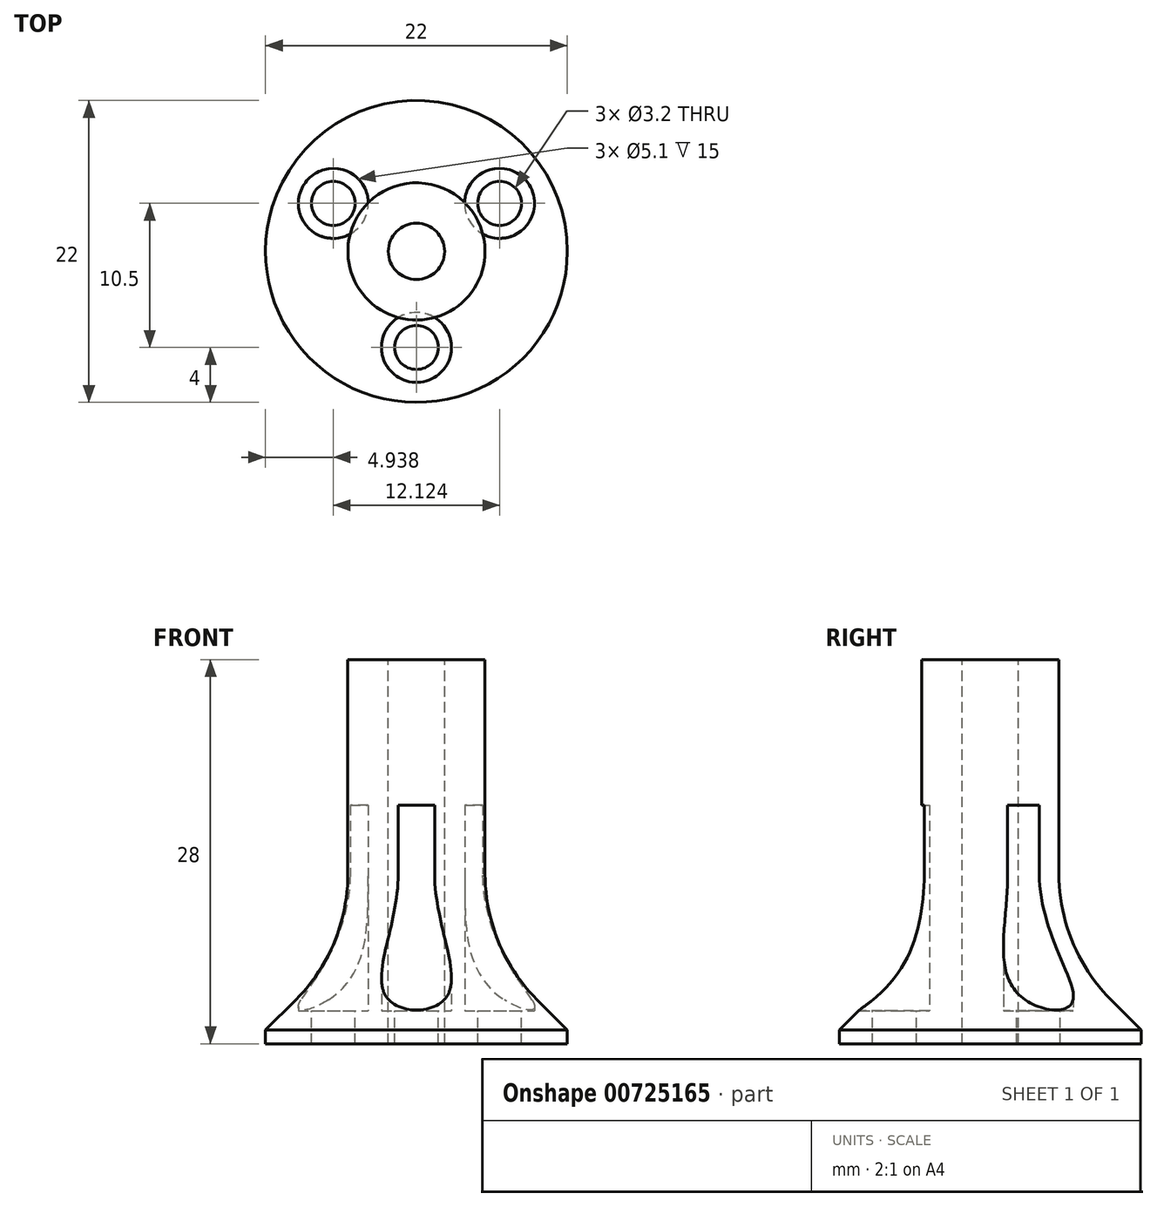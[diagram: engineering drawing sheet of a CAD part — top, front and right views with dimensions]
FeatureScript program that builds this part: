
annotation { "Feature Type Name" : "Feature", "Feature Type Description" : "" }
export const myFeature = defineFeature(function(context is Context, id is Id, definition is map)
    precondition{}
    {
        {
            var Q0;
            Q0=qCreatedBy(makeId("Top.planeOp"),FACE);
            var sketch = newSketch(context, id + "F0", { "sketchPlane" : qUnion([Q0])});
            skCircle(sketch, "E0", {"center": v(0, 0) * mm, "radius": 13 * mm});
            skSolve(sketch);
        }
        {
            var Q0;
            Q0 = qSketchRegion(id + "F0", true);
            extrude(context, id + "F1", {"entities" : qUnion([Q0]), "depth" : 6 * mm, "offsetDistance" : 25 * mm});
        }
        {
            var Q0;
            Q0=makeQuery(id+"F1.opExtrude","CAP_FACE",FACE,{"disambiguationData":[OSD([sQuery(id+"F0.wireOp",EDGE,"E0")])],"isStart":false});
            var sketch = newSketch(context, id + "F2", { "sketchPlane" : qUnion([Q0])});
            skCircle(sketch, "E1", {"center": v(0, 0) * mm, "radius": 5 * mm});
            skSolve(sketch);
        }
        {
            var Q0;
            Q0=makeQuery(id+"F2.imprint","IMPRINT",FACE,{"disambiguationData":[TD([[makeQuery(id+"F2.imprint","IMPRINT",EDGE,{"derivedFrom":sQuery(id+"F2.wireOp",EDGE,"E1")}),1.0]])]});
            extrude(context, id + "F3", {"entities" : qUnion([Q0]), "operationType" : NewBodyOperationType.ADD, "depth" : 21 * mm, "offsetDistance" : 25 * mm});
        }
        {
            var Q0;
            Q0=makeQuery(id+"F1.opExtrude","CAP_EDGE",EDGE,{"disambiguationData":[OSD([sQuery(id+"F0.wireOp",EDGE,"E0")])],"isStart":false});
            chamfer(context, id + "F4", {"entities" : qUnion([Q0]), "width" : 8 * mm, "tangentPropagation" : true});
        }
        {
            var Q0;
            Q0=makeQuery(id+"F4.opChamfer","BLEND_EDGE",EDGE,{"blendedFrom":[makeQuery(id+"F1.opExtrude","CAP_EDGE",EDGE,{"disambiguationData":[OSD([sQuery(id+"F0.wireOp",EDGE,"E0")])],"isStart":false}),makeQuery(id+"F3.opExtrude","SWEPT_FACE",FACE,{"disambiguationData":[OSD([sQuery(id+"F2.wireOp",EDGE,"E1")])]})],"blendedInto":[makeQuery(id+"F3.opExtrude","SWEPT_FACE",FACE,{"disambiguationData":[OSD([sQuery(id+"F2.wireOp",EDGE,"E1")])]})]});
            fillet(context, id + "F5", {"entities" : qUnion([Q0]), "radius" : 13 * mm, "tangentPropagation" : true, "allowEdgeOverflow" : false});
        }
        {
            var Q0;
            Q0=makeQuery(id+"F1.opExtrude","CAP_FACE",FACE,{"disambiguationData":[OSD([sQuery(id+"F0.wireOp",EDGE,"E0")])],"isStart":true});
            extrude(context, id + "F6", {"entities" : qUnion([Q0]), "operationType" : NewBodyOperationType.ADD, "depth" : 1 * mm, "offsetDistance" : 25 * mm});
        }
        {
            var Q0;
            Q0=makeQuery(id+"F6.opExtrude","CAP_FACE",FACE,{"disambiguationData":[OSD([sQuery(id+"F0.wireOp",EDGE,"E0")])],"isStart":false});
            cPlane(context, id + "F7", {"entities" : qUnion([Q0]), "cplaneType" : CPlaneType.OFFSET, "offset" : 2.4 * mm, "oppositeDirection" : true, "width" : 150 * mm, "height" : 150 * mm});
        }
        {
            var Q0;
            Q0=qCreatedBy(id+"F7.planeOp",FACE);
            var sketch = newSketch(context, id + "F8", { "sketchPlane" : qUnion([Q0])});
            skPoint(sketch, "E2", {"position": v(0, 7) * mm});
            skPoint(sketch, "E3", {"position": v(6.06, -3.5) * mm});
            skPoint(sketch, "E4", {"position": v(-6.06, -3.5) * mm});
            skCircle(sketch, "E5", {"center": v(6.06, -3.5) * mm, "radius": 1.6 * mm});
            skCircle(sketch, "E6", {"center": v(0, 7) * mm, "radius": 1.6 * mm});
            skCircle(sketch, "E7", {"center": v(-6.06, -3.5) * mm, "radius": 1.6 * mm});
            skSolve(sketch);
        }
        {
            var Q0;
            Q0 = qSketchRegion(id + "F8", true);
            extrude(context, id + "F9", {"entities" : qUnion([Q0]), "operationType" : NewBodyOperationType.REMOVE, "depth" : 25 * mm, "offsetDistance" : 25 * mm});
        }
        {
            var Q0;
            Q0=qCreatedBy(id+"F7.planeOp",FACE);
            var sketch = newSketch(context, id + "F10", { "sketchPlane" : qUnion([Q0])});
            skCircle(sketch, "E8", {"center": v(0, 7) * mm, "radius": 2.55 * mm});
            skCircle(sketch, "E9", {"center": v(6.06, -3.5) * mm, "radius": 2.55 * mm});
            skCircle(sketch, "E10", {"center": v(-6.06, -3.5) * mm, "radius": 2.55 * mm});
            skSolve(sketch);
        }
        {
            var Q0;
            Q0 = qSketchRegion(id + "F10", true);
            extrude(context, id + "F11", {"entities" : qUnion([Q0]), "operationType" : NewBodyOperationType.REMOVE, "oppositeDirection" : true, "depth" : 15 * mm, "offsetDistance" : 25 * mm});
        }
        {
            var Q0;
            Q0=makeQuery(id+"F3.opExtrude","CAP_FACE",FACE,{"disambiguationData":[OSD([sQuery(id+"F2.wireOp",EDGE,"E1")])],"isStart":false});
            var sketch = newSketch(context, id + "F12", { "sketchPlane" : qUnion([Q0])});
            skCircle(sketch, "E11", {"center": v(0, 0) * mm, "radius": 2.05 * mm});
            skSolve(sketch);
        }
        {
            var Q0;
            Q0 = qSketchRegion(id + "F12", true);
            extrude(context, id + "F13", {"entities" : qUnion([Q0]), "operationType" : NewBodyOperationType.REMOVE, "oppositeDirection" : true, "depth" : 30 * mm, "offsetDistance" : 25 * mm});
        }
    });
